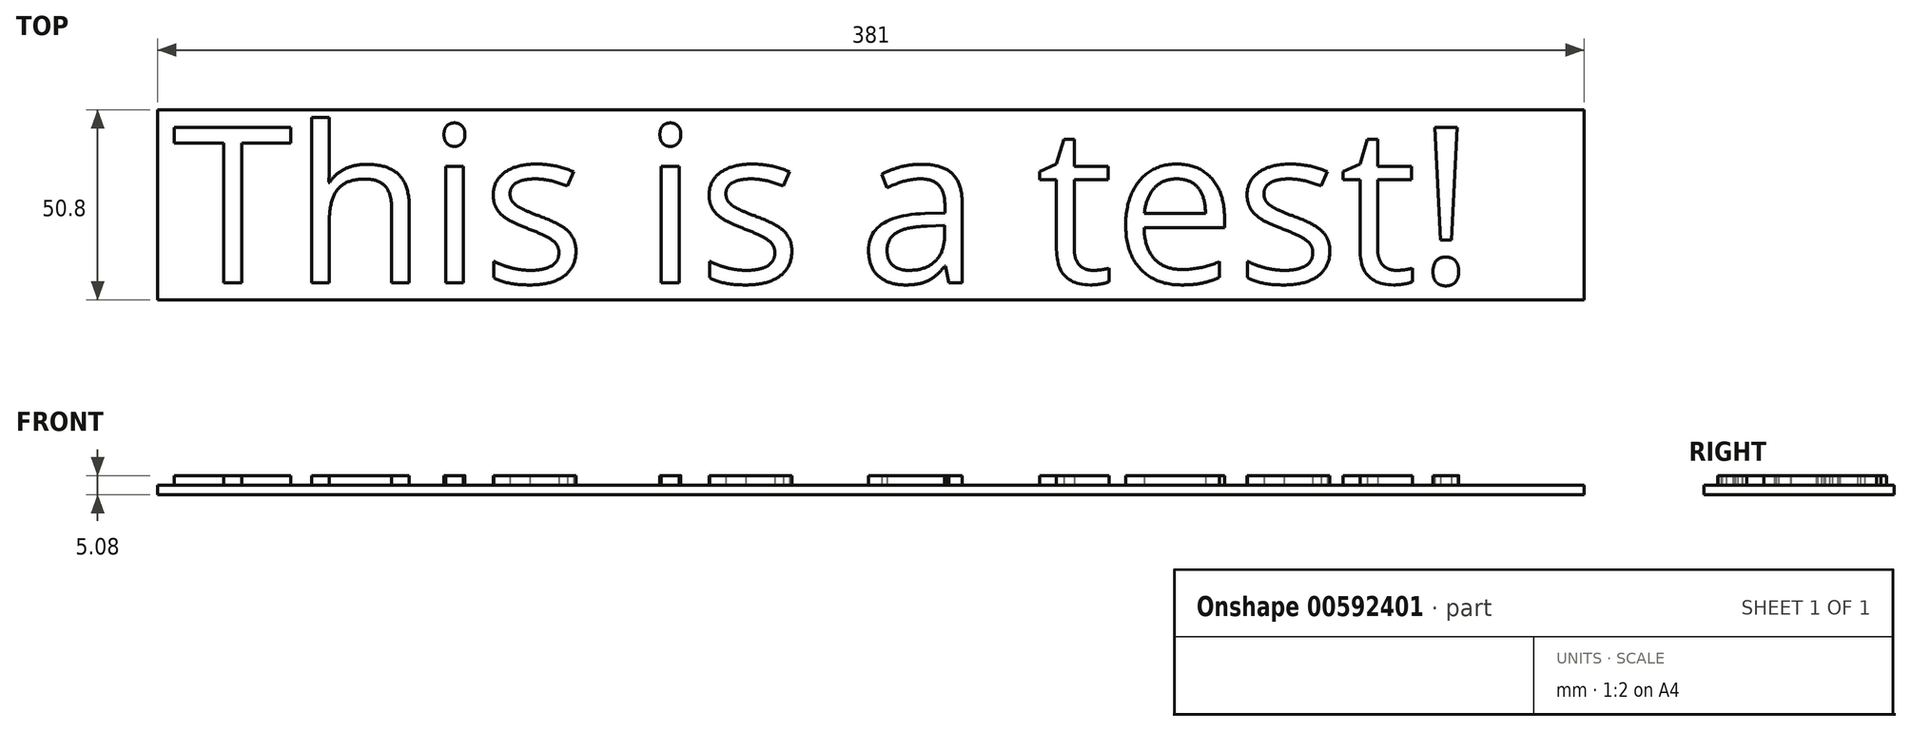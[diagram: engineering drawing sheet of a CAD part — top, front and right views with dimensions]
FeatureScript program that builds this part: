
annotation { "Feature Type Name" : "Feature", "Feature Type Description" : "" }
export const myFeature = defineFeature(function(context is Context, id is Id, definition is map)
    precondition{}
    {
        {
            var Q0;
            Q0=qCreatedBy(makeId("Top.planeOp"),FACE);
            var sketch = newSketch(context, id + "F0", { "sketchPlane" : qUnion([Q0])});
            skLineSegment(sketch, "E0.bottom", {"start": v(0, 0) * mm, "end": v(381, 0) * mm});
            skLineSegment(sketch, "E0.top", {"start": v(0, 50.8) * mm, "end": v(381, 50.8) * mm});
            skLineSegment(sketch, "E0.left", {"start": v(0, 0) * mm, "end": v(0, 50.8) * mm});
            skLineSegment(sketch, "E0.right", {"start": v(381, 0) * mm, "end": v(381, 50.8) * mm});
            skSolve(sketch);
        }
        {
            var Q0;
            Q0 = qSketchRegion(id + "F0", true);
            extrude(context, id + "F1", {"entities" : qUnion([Q0]), "depth" : 2.54 * mm, "offsetDistance" : 25.4 * mm});
        }
        {
            var Q0;
            Q0=makeQuery(id+"F1.opExtrude","CAP_FACE",FACE,{"disambiguationData":[OSD([sQuery(id+"F0.wireOp",EDGE,"E0.bottom"),sQuery(id+"F0.wireOp",EDGE,"E0.top"),sQuery(id+"F0.wireOp",EDGE,"E0.left"),sQuery(id+"F0.wireOp",EDGE,"E0.right")])],"isStart":false});
            var sketch = newSketch(context, id + "F2", { "sketchPlane" : qUnion([Q0])});
            skText(sketch, "E1", { "text": "This is a test!", "fontName": "OpenSans-Regular.ttf"});
            const initialGuessF2  = {"E1": [0.00391, 0.00455, 1, 0, 0.04194]};
            skSetInitialGuess(sketch, initialGuessF2);
            skSolve(sketch);
        }
        {
            var Q0;
            Q0 = qSketchRegion(id + "F2", true);
            extrude(context, id + "F3", {"entities" : qUnion([Q0]), "operationType" : NewBodyOperationType.ADD, "depth" : 2.54 * mm, "offsetDistance" : 25.4 * mm});
        }
    });
